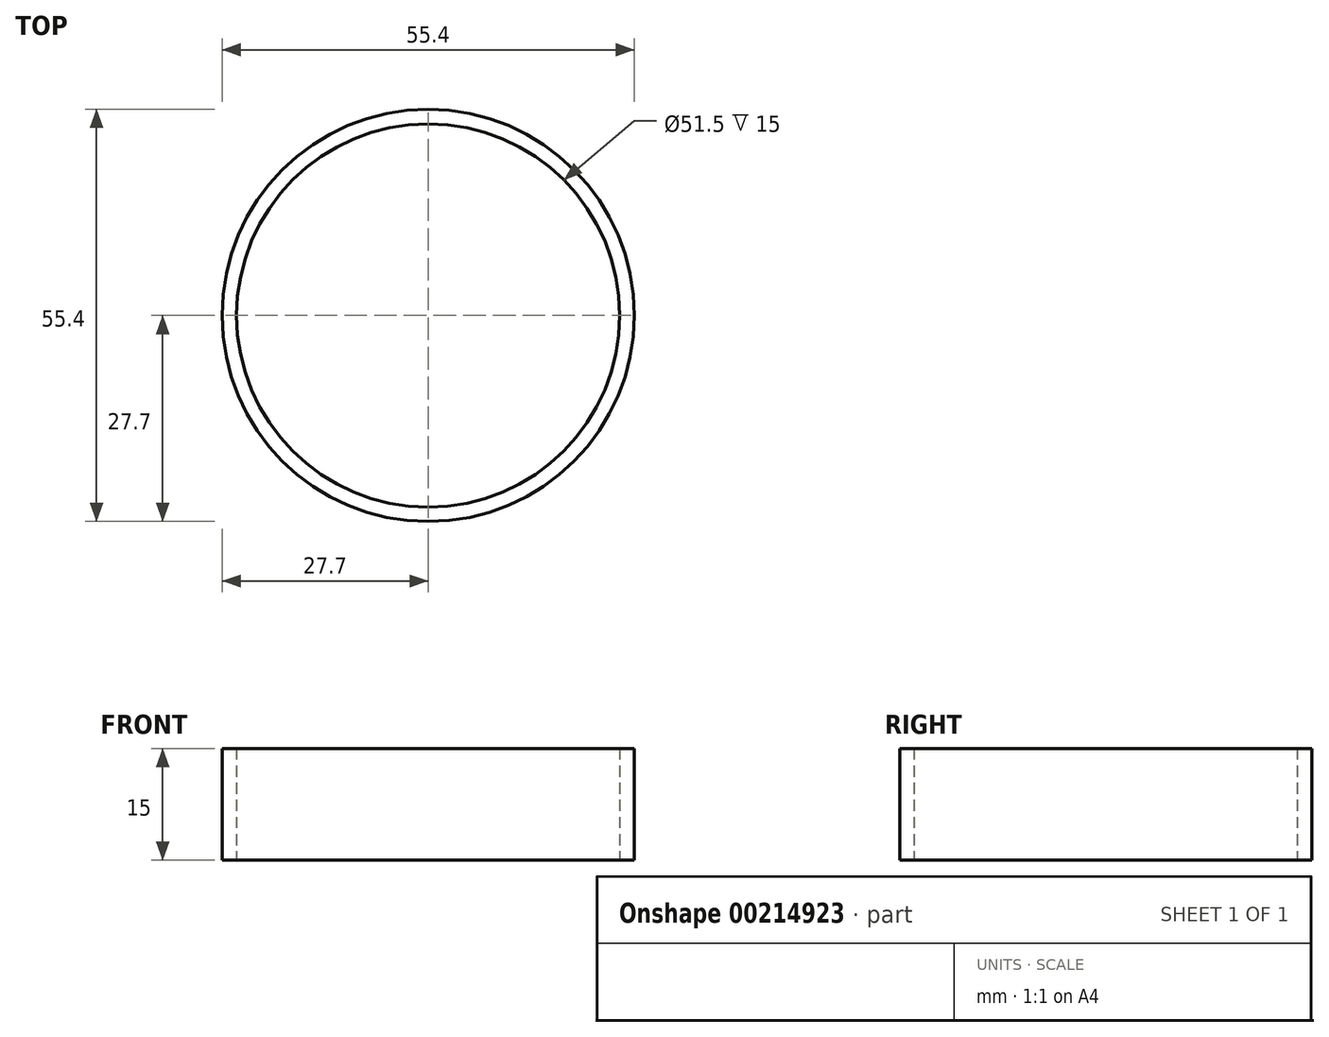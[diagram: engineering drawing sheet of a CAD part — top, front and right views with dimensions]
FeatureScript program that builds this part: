
annotation { "Feature Type Name" : "Feature", "Feature Type Description" : "" }
export const myFeature = defineFeature(function(context is Context, id is Id, definition is map)
    precondition{}
    {
        {
            var Q0;
            Q0=qCreatedBy(makeId("Top.planeOp"),FACE);
            var sketch = newSketch(context, id + "F0", { "sketchPlane" : qUnion([Q0])});
            skCircle(sketch, "E0", {"center": v(0, 0) * mm, "radius": 27.7 * mm});
            skCircle(sketch, "E1", {"center": v(0, 0) * mm, "radius": 25.75 * mm});
            skSolve(sketch);
        }
        {
            var Q0;
            Q0=makeQuery(id+"F0.imprint","IMPRINT",FACE,{"disambiguationData":[TD([[makeQuery(id+"F0.imprint","IMPRINT",EDGE,{"derivedFrom":sQuery(id+"F0.wireOp",EDGE,"E0")}),1.0]])]});
            extrude(context, id + "F1", {"entities" : qUnion([Q0]), "depth" : 15 * mm, "offsetDistance" : 25 * mm});
        }
    });
